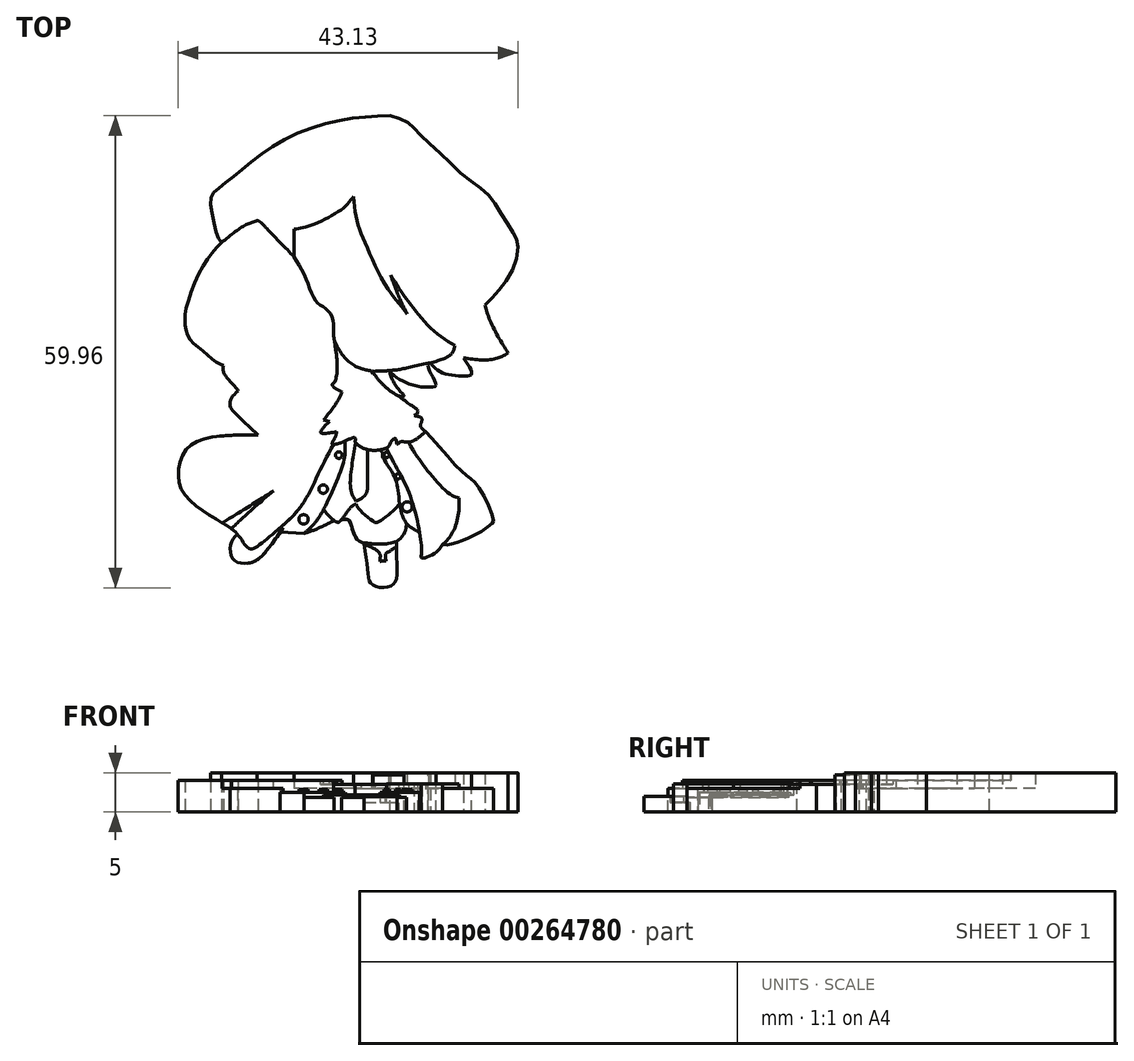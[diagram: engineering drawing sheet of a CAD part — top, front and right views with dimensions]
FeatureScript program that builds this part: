
annotation { "Feature Type Name" : "Feature", "Feature Type Description" : "" }
export const myFeature = defineFeature(function(context is Context, id is Id, definition is map)
    precondition{}
    {
        {
            var Q0;
            Q0=qCreatedBy(makeId("Top.planeOp"),FACE);
            var sketch = newSketch(context, id + "F0", { "sketchPlane" : qUnion([Q0])});
            skFitSpline(sketch, "E0", {"points": [v(4.64, 28.75) * mm, v(-1.15, 28.28) * mm, v(-8.48, 25.89) * mm, v(-13.76, 22.25) * mm, v(-16.76, 19.8) * mm, v(-18, 18.6) * mm, v(-18, 16.71) * mm, v(-17.3, 13.62) * mm, v(-16.76, 12.62) * mm], "startDerivative": vector(-35.2, -1.01) * mm, "endDerivative": vector(8.06, -11.5) * mm});
            skFitSpline(sketch, "E1", {"points": [v(4.64, 28.75) * mm, v(6.83, 27.93) * mm, v(8.08, 26.74) * mm, v(10.87, 24.14) * mm, v(14.46, 20.8) * mm, v(17.05, 18.8) * mm, v(18.75, 16.36) * mm, v(20.34, 13.82) * mm, v(20.87, 12.62) * mm, v(20.4, 9.58) * mm, v(18.5, 6.6) * mm, v(16.7, 4.7) * mm], "startDerivative": vector(29.85, -8.31) * mm, "endDerivative": vector(-20.54, -20.46) * mm});
            skFitSpline(sketch, "E2", {"points": [v(16.7, 4.7) * mm, v(17.2, 3.15) * mm, v(18.33, 0.8) * mm, v(19.68, -1.42) * mm], "startDerivative": vector(1.46, -5.18) * mm, "endDerivative": vector(3.8, -6.03) * mm});
            skFitSpline(sketch, "E3", {"points": [v(19.68, -1.42) * mm, v(17.58, -2.22) * mm, v(13.97, -2) * mm], "startDerivative": vector(-4.38, -2.29) * mm, "endDerivative": vector(-6.92, 0.99) * mm});
            skFitSpline(sketch, "E4", {"points": [v(13.97, -2) * mm, v(15.02, -4.06) * mm, v(13.97, -4.31) * mm, v(11.2, -3.85) * mm, v(9.78, -2.63) * mm], "startDerivative": vector(6.52, -9.38) * mm, "endDerivative": vector(-4.86, 5.7) * mm});
            skFitSpline(sketch, "E5", {"points": [v(9.78, -2.63) * mm, v(9.78, -3.85) * mm, v(10.47, -5.36) * mm, v(10.17, -5.69) * mm, v(7.8, -5.51) * mm, v(5.88, -4.69) * mm, v(4.64, -3.85) * mm], "startDerivative": vector(-1.49, -7.5) * mm, "endDerivative": vector(-7.08, 5.05) * mm});
            skFitSpline(sketch, "E6", {"points": [v(4.64, -3.85) * mm, v(5.08, -5.01) * mm, v(6, -6.31) * mm, v(6.46, -6.83) * mm, v(6.03, -6.9) * mm, v(5.2, -6.56) * mm, v(3.76, -5.41) * mm, v(2.5, -3.85) * mm], "startDerivative": vector(1.06, -6.43) * mm, "endDerivative": vector(-5.82, 7.97) * mm});
            skFitSpline(sketch, "E7", {"points": [v(0, 18.5) * mm, v(-1.53, 16.84) * mm, v(-5.52, 14.8) * mm, v(-7.53, 14.34) * mm], "startDerivative": vector(-4, -5.51) * mm, "endDerivative": vector(-6.25, -0.93) * mm});
            skFitSpline(sketch, "E8", {"points": [v(-7.53, 14.34) * mm, v(-7.53, 12.2) * mm, v(-7.53, 10.78) * mm], "startDerivative": vector(0, -4.1) * mm, "endDerivative": vector(0, -2.99) * mm});
            skFitSpline(sketch, "E9", {"points": [v(0, 18.5) * mm, v(0.48, 15.42) * mm, v(1.45, 12.73) * mm, v(3.73, 7.84) * mm, v(6.85, 3.57) * mm], "startDerivative": vector(1.71, -14.72) * mm, "endDerivative": vector(11.53, -14.1) * mm});
            skFitSpline(sketch, "E10", {"points": [v(6.85, 3.57) * mm, v(5.88, 5.54) * mm, v(4.73, 8.54) * mm], "startDerivative": vector(-2.16, 4.1) * mm, "endDerivative": vector(-2.07, 5.78) * mm});
            skFitSpline(sketch, "E11", {"points": [v(4.73, 8.54) * mm, v(6.2, 6.2) * mm, v(7.9, 3.96) * mm, v(10.12, 1.5) * mm, v(12.69, -0.3) * mm, v(14.43, -1.02) * mm], "startDerivative": vector(7.16, -11.83) * mm, "endDerivative": vector(10.1, -3.6) * mm});
            skFitSpline(sketch, "E12", {"points": [v(14.43, -1.02) * mm, v(13.9, 1.72) * mm, v(13.69, 3.12) * mm], "startDerivative": vector(-1, 5.08) * mm, "endDerivative": vector(-0.47, 3.08) * mm});
            skFitSpline(sketch, "E13", {"points": [v(13.83, 2.2) * mm, v(14.8, 1.45) * mm, v(16.53, 0.57) * mm], "startDerivative": vector(2, -1.71) * mm, "endDerivative": vector(3.34, -1.54) * mm});
            skFitSpline(sketch, "E14", {"points": [v(12.9, -0.4) * mm, v(12.41, -1.55) * mm, v(9.78, -2.63) * mm, v(5.88, -3.5) * mm, v(4.5, -3.63) * mm], "startDerivative": vector(-1.37, -6.6) * mm, "endDerivative": vector(-6.04, -0.38) * mm});
            skFitSpline(sketch, "E15", {"points": [v(4.64, -3.85) * mm, v(4.5, -3.63) * mm], "startDerivative": vector(-0.14, 0.22) * mm, "endDerivative": vector(-0.14, 0.22) * mm});
            skFitSpline(sketch, "E16", {"points": [v(4.5, -3.63) * mm, v(2.81, -3.7) * mm, v(2.45, -3.7) * mm], "startDerivative": vector(-2.92, -0.14) * mm, "endDerivative": vector(-0.94, 0.02) * mm});
            skFitSpline(sketch, "E17", {"points": [v(2.5, -3.85) * mm, v(2.45, -3.7) * mm], "startDerivative": vector(-0.04, 0.14) * mm, "endDerivative": vector(-0.04, 0.14) * mm});
            skFitSpline(sketch, "E18", {"points": [v(2.45, -3.7) * mm, v(1, -3.37) * mm, v(-0.99, -2.1) * mm, v(-2.34, 0) * mm, v(-2.42, 0.26) * mm, v(-2.5, 0.86) * mm], "startDerivative": vector(-6.7, 1.33) * mm, "endDerivative": vector(-0.3, 5.17) * mm});
            skFitSpline(sketch, "E19", {"points": [v(-2.5, 0.86) * mm, v(-2.5, 1.74) * mm, v(-2.76, 3.31) * mm, v(-3.77, 4.43) * mm, v(-4.85, 5.32) * mm, v(-6, 8) * mm, v(-7.53, 10.78) * mm, v(-9.09, 12.43) * mm, v(-10.9, 14.33) * mm, v(-11.48, 14.95) * mm, v(-12.22, 15.42) * mm], "startDerivative": vector(0.15, 11.14) * mm, "endDerivative": vector(-6.01, -4.13) * mm});
            skFitSpline(sketch, "E20", {"points": [v(-12.22, 15.42) * mm, v(-13.92, 14.74) * mm, v(-16.76, 12.62) * mm], "startDerivative": vector(-3.9, -1.2) * mm, "endDerivative": vector(-5.1, -4.23) * mm});
            skFitSpline(sketch, "E21", {"points": [v(-16.76, 12.62) * mm, v(-19.1, 9.65) * mm, v(-21.19, 4.46) * mm, v(-21.36, 2.17) * mm, v(-20.87, 0.51) * mm, v(-19.28, -0.97) * mm, v(-17.48, -2.47) * mm, v(-16.51, -2.98) * mm], "startDerivative": vector(-13.81, -14.7) * mm, "endDerivative": vector(9.8, -4.22) * mm});
            skFitSpline(sketch, "E22", {"points": [v(-16.51, -2.98) * mm, v(-16.51, -3.71) * mm, v(-15.97, -4.63) * mm, v(-14.72, -6.03) * mm, v(-14.3, -6.84) * mm, v(-14.16, -7.62) * mm], "startDerivative": vector(-0.5, -4.39) * mm, "endDerivative": vector(0.62, -4.57) * mm});
            skFitSpline(sketch, "E23", {"points": [v(-14.62, -6.18) * mm, v(-15.58, -7.28) * mm, v(-15.62, -8.19) * mm, v(-15.2, -8.81) * mm, v(-14.09, -9.93) * mm, v(-12.13, -11.8) * mm], "startDerivative": vector(-5.87, -5.15) * mm, "endDerivative": vector(7.41, -7.05) * mm});
            skFitSpline(sketch, "E24", {"points": [v(-12.13, -11.8) * mm, v(-14.56, -11.8) * mm, v(-18.73, -12.25) * mm, v(-21.2, -13.6) * mm, v(-22.17, -16.09) * mm, v(-21.84, -18.7) * mm, v(-19.67, -21.03) * mm, v(-16.76, -22.9) * mm, v(-14.56, -24.6) * mm, v(-13.17, -26.29) * mm, v(-11.3, -25.24) * mm, v(-6.96, -21.25) * mm, v(-4.17, -16.16) * mm, v(-1.46, -10.56) * mm, v(-0.58, -6.65) * mm], "startDerivative": vector(-37.16, 0.62) * mm, "endDerivative": vector(7.21, 49.15) * mm});
            skFitSpline(sketch, "E25", {"points": [v(-0.58, -6.65) * mm, v(-2.34, 0) * mm], "startDerivative": vector(-1.76, 6.65) * mm, "endDerivative": vector(-1.76, 6.65) * mm});
            skFitSpline(sketch, "E26", {"points": [v(5.2, -6.56) * mm, v(7.5, -9.23) * mm, v(8.63, -9.61) * mm, v(8.63, -10.23) * mm, v(8.5, -10.63) * mm, v(9.43, -11.65) * mm, v(13.44, -16.1) * mm, v(14.88, -17.31) * mm, v(16.24, -18.94) * mm, v(17.82, -22.63) * mm, v(17.58, -23.1) * mm, v(15.58, -24.42) * mm, v(13.75, -25.24) * mm, v(12.28, -25.72) * mm, v(11.34, -25.72) * mm], "startDerivative": vector(22.11, -34.49) * mm, "endDerivative": vector(-17.24, 1.6) * mm});
            skFitSpline(sketch, "E27", {"points": [v(11.34, -25.72) * mm, v(10.38, -26.8) * mm, v(8.7, -27.42) * mm, v(8.65, -26.96) * mm, v(8.4, -24.04) * mm, v(6.68, -18.2) * mm, v(4.23, -13.53) * mm, v(1, -3.37) * mm], "startDerivative": vector(-7.19, -11.67) * mm, "endDerivative": vector(-12.38, 45.63) * mm});
            skFitSpline(sketch, "E28", {"points": [v(11.34, -25.72) * mm, v(12.16, -24.9) * mm, v(13.2, -22.66) * mm, v(13.45, -19.83) * mm], "startDerivative": vector(3.27, 2.7) * mm, "endDerivative": vector(0.06, 7.34) * mm});
            skFitSpline(sketch, "E29", {"points": [v(13.45, -19.83) * mm, v(12.34, -19.36) * mm, v(9.74, -16.71) * mm, v(7.36, -13.34) * mm, v(2.33, -3.68) * mm], "startDerivative": vector(-7.77, 2.03) * mm, "endDerivative": vector(-13.93, 27.93) * mm});
            skFitSpline(sketch, "E30", {"points": [v(-2.45, 0.44) * mm, v(-2.05, -3.03) * mm, v(-2.31, -4.91) * mm, v(-2.72, -5.42) * mm], "startDerivative": vector(1.24, -7.85) * mm, "endDerivative": vector(-2.26, -2.02) * mm});
            skFitSpline(sketch, "E31", {"points": [v(-2.72, -5.42) * mm, v(-2.34, -5.85) * mm, v(-1.44, -6.32) * mm], "startDerivative": vector(0.75, -1.04) * mm, "endDerivative": vector(1.78, -0.78) * mm});
            skFitSpline(sketch, "E32", {"points": [v(-1.44, -6.32) * mm, v(-2, -7.48) * mm, v(-3.76, -9.9) * mm], "startDerivative": vector(-1.13, -2.7) * mm, "endDerivative": vector(-3.36, -4.35) * mm});
            skFitSpline(sketch, "E33", {"points": [v(-3.76, -9.9) * mm, v(-3, -10.06) * mm], "startDerivative": vector(0.75, -0.16) * mm, "endDerivative": vector(0.75, -0.16) * mm});
            skFitSpline(sketch, "E34", {"points": [v(-3, -10.06) * mm, v(-3.93, -11.03) * mm, v(-4.14, -11.5) * mm, v(-3.76, -11.6) * mm, v(-2.1, -11.38) * mm], "startDerivative": vector(-3.38, -3.26) * mm, "endDerivative": vector(5.48, 1) * mm});
            skFitSpline(sketch, "E35", {"points": [v(-2.1, -11.38) * mm, v(-2.44, -12.36) * mm, v(-2.7, -12.92) * mm, v(-1.52, -12.77) * mm, v(0.19, -12.16) * mm, v(0.27, -12.46) * mm, v(0.22, -12.62) * mm, v(1.68, -13.63) * mm, v(4.4, -13.34) * mm, v(4.69, -12.84) * mm, v(5.32, -12.23) * mm, v(5.47, -12.67) * mm, v(5.61, -12.97) * mm, v(5.96, -12.7) * mm, v(7, -12.7) * mm, v(8.57, -11.9) * mm, v(9.82, -10.47) * mm, v(9.68, -10.31) * mm], "startDerivative": vector(-3.85, -15.8) * mm, "endDerivative": vector(-7.4, 3.88) * mm});
            skFitSpline(sketch, "E36", {"points": [v(9.68, -10.31) * mm, v(8.98, -10.31) * mm, v(7.23, -10) * mm, v(6.43, -9.7) * mm], "startDerivative": vector(-2.2, -0.14) * mm, "endDerivative": vector(-2.27, 0.96) * mm});
            skFitSpline(sketch, "E37", {"points": [v(6.4, -9.7) * mm, v(7.06, -9.46) * mm, v(8.04, -9.14) * mm, v(8.15, -8.64) * mm, v(7.57, -8.17) * mm, v(5.73, -6.83) * mm], "startDerivative": vector(3.4, 1.59) * mm, "endDerivative": vector(-6.64, 5.1) * mm});
            skFitSpline(sketch, "E38", {"points": [v(-1.44, -6.32) * mm, v(-0.6, -4.07) * mm, v(-0.42, -3.64) * mm, v(2.26, -3.9) * mm, v(2.8, -4.27) * mm], "startDerivative": vector(3.4, 7.98) * mm, "endDerivative": vector(1.85, -2.14) * mm});
            skFitSpline(sketch, "E39", {"points": [v(-9.93, -24.12) * mm, v(-6.25, -24.29) * mm], "startDerivative": vector(3.69, -0.17) * mm, "endDerivative": vector(3.69, -0.17) * mm});
            skFitSpline(sketch, "E40", {"points": [v(-6.25, -24.29) * mm, v(-4.6, -22.6) * mm, v(-2.34, -18.2) * mm, v(-1.08, -14.43) * mm, v(-1.08, -12.58) * mm], "startDerivative": vector(7.6, 6.43) * mm, "endDerivative": vector(-0.8, 8.96) * mm});
            skFitSpline(sketch, "E41", {"points": [v(3.37, -13.69) * mm, v(3.72, -14.15) * mm, v(3.7, -14.48) * mm, v(5.04, -16.72) * mm, v(5.73, -19.28) * mm, v(6.56, -22.74) * mm, v(8.43, -24.17) * mm], "startDerivative": vector(5.17, -5.25) * mm, "endDerivative": vector(11.12, -5.53) * mm});
            skFitSpline(sketch, "E42", {"points": [v(-3.76, -21.23) * mm, v(-3.15, -22.03) * mm, v(-2.05, -22.88) * mm, v(-1.52, -22.58) * mm, v(-0.22, -20.9) * mm, v(0.32, -20.56) * mm], "startDerivative": vector(2.47, -3.74) * mm, "endDerivative": vector(2.9, 1.37) * mm});
            skFitSpline(sketch, "E43", {"points": [v(0.32, -20.56) * mm, v(0.86, -21.38) * mm, v(2.7, -22.88) * mm, v(3.12, -22.88) * mm, v(4.77, -21.7) * mm, v(5.9, -20.56) * mm], "startDerivative": vector(2.06, -4.3) * mm, "endDerivative": vector(4.48, 5.02) * mm});
            skFitSpline(sketch, "E44", {"points": [v(0.32, -20.56) * mm, v(-0.2, -19.43) * mm, v(-0.22, -17.63) * mm, v(0, -14.09) * mm, v(0.22, -12.62) * mm], "startDerivative": vector(-3.18, 5.39) * mm, "endDerivative": vector(1.1, 5.7) * mm});
            skFitSpline(sketch, "E45", {"points": [v(1.84, -13.67) * mm, v(1.68, -19.06) * mm, v(1.23, -19.88) * mm, v(0.32, -20.56) * mm], "startDerivative": vector(0.2, -12.39) * mm, "endDerivative": vector(-4.1, -2.8) * mm});
            skFitSpline(sketch, "E46", {"points": [v(-6.25, -24.29) * mm, v(-4.72, -23.77) * mm, v(-2.46, -22.66) * mm], "startDerivative": vector(3.28, 1) * mm, "endDerivative": vector(4.25, 2.21) * mm});
            skFitSpline(sketch, "E47", {"points": [v(-1.52, -22.58) * mm, v(-0.63, -22.58) * mm, v(-0.2, -23.51) * mm, v(0.44, -25.02) * mm, v(1.44, -25.5) * mm, v(5.66, -25.22) * mm, v(6.72, -23.47) * mm, v(6.77, -23.02) * mm], "startDerivative": vector(10.67, 1.95) * mm, "endDerivative": vector(0.05, 4.54) * mm});
            skSolve(sketch);
        }
        {
            var Q0;
            Q0=makeQuery(id+"F0.imprint","IMPRINT",FACE,{"disambiguationData":[TD([[makeQuery(id+"F0.imprint","IMPRINT",EDGE,{"derivedFrom":sQuery(id+"F0.wireOp",EDGE,"E7")}),1.0]])]});
            extrude(context, id + "F1", {"entities" : qUnion([Q0]), "depth" : 3 * mm, "offsetDistance" : 25 * mm});
        }
        {
            var Q0;
            Q0=makeQuery(id+"F0.imprint","IMPRINT",FACE,{"disambiguationData":[TD([[makeQuery(id+"F0.imprint","IMPRINT",EDGE,{"derivedFrom":sQuery(id+"F0.wireOp",EDGE,"E0")}),1.0]])]});
            extrude(context, id + "F2", {"entities" : qUnion([Q0]), "operationType" : NewBodyOperationType.ADD, "depth" : 5 * mm, "offsetDistance" : 25 * mm});
        }
        {
            var Q0;
            {var subQ0=sQuery(id+"F0.wireOp",EDGE,"E20");Q0=makeQuery(id+"F0.imprint","IMPRINT",FACE,{"disambiguationData":[TD([[makeQuery(id+"F0.imprint","IMPRINT",EDGE,{"derivedFrom":subQ0}),1.0]])]});}
            var Q1;
            {var subQ0=sQuery(id+"F0.wireOp",EDGE,"E27");Q1=makeQuery(id+"F0.imprint","IMPRINT",FACE,{"disambiguationData":[TD([[makeQuery(id+"F0.imprint","IMPRINT",EDGE,{"derivedFrom":subQ0}),-1.0]])]});}
            extrude(context, id + "F3", {"entities" : qUnion([Q0, Q1]), "operationType" : NewBodyOperationType.ADD, "depth" : 4 * mm, "offsetDistance" : 25 * mm});
        }
        {
            var Q0;
            {var subQ0=sQuery(id+"F0.wireOp",EDGE,"E28");Q0=makeQuery(id+"F0.imprint","IMPRINT",FACE,{"disambiguationData":[TD([[makeQuery(id+"F0.imprint","IMPRINT",EDGE,{"derivedFrom":subQ0}),-1.0]])]});}
            var Q1;
            {var subQ1=sQuery(id+"F0.wireOp",EDGE,"E17");Q1=makeQuery(id+"F0.imprint","IMPRINT",FACE,{"disambiguationData":[TD([[makeQuery(id+"F0.imprint","IMPRINT",EDGE,{"derivedFrom":subQ1}),1.0]])]});}
            extrude(context, id + "F4", {"entities" : qUnion([Q0, Q1]), "operationType" : NewBodyOperationType.ADD, "depth" : 3 * mm, "offsetDistance" : 25 * mm});
        }
        {
            var Q0;
            {var subQ5=sQuery(id+"F0.wireOp",EDGE,"E25");var subQ6=sQuery(id+"F0.wireOp",EDGE,"E24");var subQ7=makeQuery(id+"F0.imprint","INTERSECT",VERTEX,{"derivedFrom":[subQ6,subQ5]});Q0=makeQuery(id+"F0.imprint","IMPRINT",FACE,{"disambiguationData":[TD([[makeQuery(id+"F0.imprint","IMPRINT",EDGE,{"disambiguationData":[TD([[subQ7,1.0]])],"derivedFrom":subQ6}),-1.0]])]});}
            var Q1;
            {var subQ0=sQuery(id+"F0.wireOp",EDGE,"E32");Q1=makeQuery(id+"F0.imprint","IMPRINT",FACE,{"disambiguationData":[TD([[makeQuery(id+"F0.imprint","IMPRINT",EDGE,{"derivedFrom":subQ0}),1.0]])]});}
            var Q2;
            Q2=makeQuery(id+"F3.opExtrude","CAP_FACE",FACE,{"disambiguationData":[OSD([sQuery(id+"F0.wireOp",EDGE,"E18"),sQuery(id+"F0.wireOp",EDGE,"E27"),sQuery(id+"F0.wireOp",EDGE,"E28"),sQuery(id+"F0.wireOp",EDGE,"E29")])],"isStart":false});
            var Q3;
            {var subQ0=sQuery(id+"F0.wireOp",EDGE,"E26");var subQ5=sQuery(id+"F0.wireOp",EDGE,"E6");var subQ6=makeQuery(id+"F0.imprint","INTERSECT",VERTEX,{"derivedFrom":[subQ5,subQ0]});Q3=makeQuery(id+"F0.imprint","IMPRINT",FACE,{"disambiguationData":[TD([[makeQuery(id+"F0.imprint","IMPRINT",EDGE,{"disambiguationData":[TD([[subQ6,-1.0]])],"derivedFrom":subQ5}),1.0]])]});}
            var Q4;
            {var subQ0=sQuery(id+"F0.wireOp",EDGE,"E26");var subQ1=sQuery(id+"F0.wireOp",EDGE,"E6");var subQ2=makeQuery(id+"F0.imprint","INTERSECT",VERTEX,{"derivedFrom":[subQ1,subQ0]});Q4=makeQuery(id+"F0.imprint","IMPRINT",FACE,{"disambiguationData":[TD([[makeQuery(id+"F0.imprint","IMPRINT",EDGE,{"disambiguationData":[TD([[subQ2,1.0]])],"derivedFrom":subQ1}),1.0]])]});}
            var Q5;
            {var subQ4=sQuery(id+"F0.wireOp",EDGE,"E30");Q5=makeQuery(id+"F0.imprint","IMPRINT",FACE,{"disambiguationData":[TD([[makeQuery(id+"F0.imprint","IMPRINT",EDGE,{"derivedFrom":subQ4}),1.0]])]});}
            var Q6;
            {var subQ0=sQuery(id+"F0.wireOp",EDGE,"E25");var subQ1=sQuery(id+"F0.wireOp",EDGE,"E18");var subQ2=makeQuery(id+"F0.imprint","INTERSECT",VERTEX,{"derivedFrom":[subQ1,subQ0]});Q6=makeQuery(id+"F0.imprint","IMPRINT",FACE,{"disambiguationData":[TD([[makeQuery(id+"F0.imprint","IMPRINT",EDGE,{"disambiguationData":[TD([[subQ2,1.0]])],"derivedFrom":subQ1}),1.0]])]});}
            extrude(context, id + "F5", {"entities" : qUnion([Q0, Q1, Q2, Q3, Q4, Q5, Q6]), "operationType" : NewBodyOperationType.ADD, "depth" : 5 * mm, "offsetDistance" : 25 * mm});
        }
        {
            var Q0;
            Q0=makeQuery(id+"F5.opExtrude","CAP_FACE",FACE,{"disambiguationData":[OSD([sQuery(id+"F0.wireOp",EDGE,"E18"),sQuery(id+"F0.wireOp",EDGE,"E27"),sQuery(id+"F0.wireOp",EDGE,"E28"),sQuery(id+"F0.wireOp",EDGE,"E29")])],"isStart":false});
            extrude(context, id + "F6", {"entities" : qUnion([Q0]), "operationType" : NewBodyOperationType.REMOVE, "oppositeDirection" : true, "depth" : 5.4 * mm, "offsetDistance" : 25 * mm});
        }
        {
            var Q0;
            {var subQ0=sQuery(id+"F0.wireOp",EDGE,"E35");var subQ1=sQuery(id+"F0.wireOp",EDGE,"E27");var subQ2=makeQuery(id+"F0.imprint","INTERSECT",VERTEX,{"derivedFrom":[subQ1,subQ0]});Q0=makeQuery(id+"F0.imprint","IMPRINT",FACE,{"disambiguationData":[TD([[makeQuery(id+"F0.imprint","IMPRINT",EDGE,{"disambiguationData":[TD([[subQ2,-1.0]])],"derivedFrom":subQ1}),-1.0]])]});}
            extrude(context, id + "F7", {"entities" : qUnion([Q0]), "operationType" : NewBodyOperationType.ADD, "depth" : 5 * mm, "offsetDistance" : 25 * mm});
        }
        {
            var Q0;
            {var subQ0=sQuery(id+"F0.wireOp",EDGE,"E39");Q0=makeQuery(id+"F0.imprint","IMPRINT",FACE,{"disambiguationData":[TD([[makeQuery(id+"F0.imprint","IMPRINT",EDGE,{"derivedFrom":subQ0}),1.0]])]});}
            var Q1;
            {var subQ0=sQuery(id+"F0.wireOp",EDGE,"E41");var subQ5=sQuery(id+"F0.wireOp",EDGE,"E27");var subQ7=makeQuery(id+"F0.imprint","INTERSECT",VERTEX,{"derivedFrom":[subQ5,subQ0]});Q1=makeQuery(id+"F0.imprint","IMPRINT",FACE,{"disambiguationData":[TD([[makeQuery(id+"F0.imprint","IMPRINT",EDGE,{"disambiguationData":[TD([[subQ7,-1.0]])],"derivedFrom":subQ5}),1.0]])]});}
            extrude(context, id + "F8", {"entities" : qUnion([Q0, Q1]), "operationType" : NewBodyOperationType.ADD, "depth" : 2.5 * mm, "offsetDistance" : 25 * mm});
        }
        {
            var Q0;
            {var subQ0=sQuery(id+"F0.wireOp",EDGE,"E46");Q0=makeQuery(id+"F0.imprint","IMPRINT",FACE,{"disambiguationData":[TD([[makeQuery(id+"F0.imprint","IMPRINT",EDGE,{"derivedFrom":subQ0}),1.0]])]});}
            var Q1;
            {var subQ0=sQuery(id+"F0.wireOp",EDGE,"E43");Q1=makeQuery(id+"F0.imprint","IMPRINT",FACE,{"disambiguationData":[TD([[makeQuery(id+"F0.imprint","IMPRINT",EDGE,{"derivedFrom":subQ0}),-1.0]])]});}
            extrude(context, id + "F9", {"entities" : qUnion([Q0, Q1]), "operationType" : NewBodyOperationType.ADD, "depth" : 1.9 * mm, "offsetDistance" : 25 * mm});
        }
        {
            var Q0;
            {var subQ7=sQuery(id+"F0.wireOp",EDGE,"E44");Q0=makeQuery(id+"F0.imprint","IMPRINT",FACE,{"disambiguationData":[TD([[makeQuery(id+"F0.imprint","IMPRINT",EDGE,{"derivedFrom":subQ7}),1.0]])]});}
            var Q1;
            {var subQ0=sQuery(id+"F0.wireOp",EDGE,"E44");Q1=makeQuery(id+"F0.imprint","IMPRINT",FACE,{"disambiguationData":[TD([[makeQuery(id+"F0.imprint","IMPRINT",EDGE,{"derivedFrom":subQ0}),-1.0]])]});}
            var Q2;
            {var subQ4=sQuery(id+"F0.wireOp",EDGE,"E43");Q2=makeQuery(id+"F0.imprint","IMPRINT",FACE,{"disambiguationData":[TD([[makeQuery(id+"F0.imprint","IMPRINT",EDGE,{"derivedFrom":subQ4}),1.0]])]});}
            extrude(context, id + "F10", {"entities" : qUnion([Q0, Q1, Q2]), "operationType" : NewBodyOperationType.ADD, "depth" : 2.2 * mm, "offsetDistance" : 25 * mm});
        }
        {
            var Q0;
            Q0=makeQuery(id+"F10.opExtrude","CAP_FACE",FACE,{"disambiguationData":[OSD([sQuery(id+"F0.wireOp",EDGE,"E35"),sQuery(id+"F0.wireOp",EDGE,"E40"),sQuery(id+"F0.wireOp",EDGE,"E41"),sQuery(id+"F0.wireOp",EDGE,"E42"),sQuery(id+"F0.wireOp",EDGE,"E43")])],"isStart":false});
            var sketch = newSketch(context, id + "F11", { "sketchPlane" : qUnion([Q0])});
            skFitSpline(sketch, "E48", {"points": [v(0.31, -12.79) * mm, v(0, -14.3) * mm, v(-0.3, -18.86) * mm, v(0.32, -20.56) * mm], "startDerivative": vector(-1.12, -4.6) * mm, "endDerivative": vector(2.78, -4.78) * mm, "construction": true});
            skFitSpline(sketch, "E49", {"points": [v(0.32, -20.56) * mm, v(1.37, -19.7) * mm, v(1.74, -18.65) * mm, v(1.78, -13.66) * mm], "startDerivative": vector(4.62, 3.23) * mm, "endDerivative": vector(-0.2, 11.8) * mm, "construction": true});
            skFitSpline(sketch, "E50", {"points": [v(1.78, -13.66) * mm, v(1.32, -13.5) * mm, v(0.7, -13.15) * mm, v(0.31, -12.79) * mm], "startDerivative": vector(-1.43, 0.4) * mm, "endDerivative": vector(-1.08, 1.14) * mm});
            skFitSpline(sketch, "E51", {"points": [v(0.31, -12.79) * mm, v(-0.24, -16.09) * mm, v(-0.3, -18.86) * mm, v(0.31, -20.22) * mm], "startDerivative": vector(-1.58, -8.5) * mm, "endDerivative": vector(2.92, -4.7) * mm});
            skFitSpline(sketch, "E52", {"points": [v(0.31, -20.22) * mm, v(1.6, -19.29) * mm, v(1.8, -17.41) * mm, v(1.78, -13.66) * mm], "startDerivative": vector(5.65, 2.8) * mm, "endDerivative": vector(0.11, 9.44) * mm});
            skSolve(sketch);
        }
        {
            var Q0;
            {var subQ0=sQuery(id+"F11.wireOp",EDGE,"E51");Q0=makeQuery(id+"F11.imprint","IMPRINT",FACE,{"disambiguationData":[TD([[makeQuery(id+"F11.imprint","IMPRINT",EDGE,{"derivedFrom":subQ0}),1.0]])]});}
            extrude(context, id + "F12", {"entities" : qUnion([Q0]), "operationType" : NewBodyOperationType.REMOVE, "oppositeDirection" : true, "depth" : .3 * mm, "offsetDistance" : 25 * mm});
        }
        {
            var Q0;
            Q0=qCreatedBy(makeId("Top.planeOp"),FACE);
            var sketch = newSketch(context, id + "F13", { "sketchPlane" : qUnion([Q0])});
            skFitSpline(sketch, "E53", {"points": [v(9.52, -2.65) * mm, v(9.76, -3.8) * mm, v(10.5, -5.37) * mm, v(10.18, -5.68) * mm, v(7.75, -5.53) * mm, v(5.85, -4.72) * mm, v(4.63, -3.84) * mm, v(4.5, -3.63) * mm], "startDerivative": vector(-1.3, -7.93) * mm, "endDerivative": vector(-1.34, 2.86) * mm});
            skFitSpline(sketch, "E54", {"points": [v(4.5, -3.63) * mm, v(5.85, -3.47) * mm, v(9.52, -2.65) * mm], "startDerivative": vector(3.2, 0.24) * mm, "endDerivative": vector(6.92, 1.68) * mm});
            skFitSpline(sketch, "E55", {"points": [v(4.63, -3.84) * mm, v(5.06, -4.99) * mm, v(6.05, -6.32) * mm, v(6.48, -6.85) * mm, v(6.01, -6.9) * mm, v(4.39, -5.92) * mm, v(2.46, -3.69) * mm], "startDerivative": vector(2.06, -7.14) * mm, "endDerivative": vector(-7.59, 9.82) * mm});
            skFitSpline(sketch, "E56", {"points": [v(2.46, -3.69) * mm, v(4.5, -3.63) * mm], "startDerivative": vector(2.03, 0.06) * mm, "endDerivative": vector(2.03, 0.06) * mm});
            skSolve(sketch);
        }
        {
            var Q0;
            {var subQ5=sQuery(id+"F0.wireOp",EDGE,"E15");Q0=makeQuery(id+"F0.imprint","IMPRINT",FACE,{"disambiguationData":[TD([[makeQuery(id+"F0.imprint","IMPRINT",EDGE,{"derivedFrom":subQ5}),1.0]])]});}
            extrude(context, id + "F14", {"entities" : qUnion([Q0]), "operationType" : NewBodyOperationType.ADD, "depth" : 4.7 * mm, "offsetDistance" : 25 * mm});
        }
        {
            var Q0;
            Q0=qCreatedBy(makeId("Top.planeOp"),FACE);
            var sketch = newSketch(context, id + "F15", { "sketchPlane" : qUnion([Q0])});
            skFitSpline(sketch, "E57", {"points": [v(1, -3.37) * mm, v(1.66, -3.54) * mm, v(2.34, -3.67) * mm], "startDerivative": vector(1.3, -0.37) * mm, "endDerivative": vector(1.36, -0.24) * mm});
            skFitSpline(sketch, "E58", {"points": [v(2.34, -3.67) * mm, v(2.53, -4.06) * mm], "startDerivative": vector(0.2, -0.39) * mm, "endDerivative": vector(0.2, -0.39) * mm});
            skFitSpline(sketch, "E59", {"points": [v(1, -3.37) * mm, v(1.05, -3.74) * mm], "startDerivative": vector(0.05, -0.38) * mm, "endDerivative": vector(0.05, -0.38) * mm});
            skFitSpline(sketch, "E60", {"points": [v(1.05, -3.74) * mm, v(2.53, -4.06) * mm], "startDerivative": vector(1.48, -0.31) * mm, "endDerivative": vector(1.48, -0.31) * mm});
            skSolve(sketch);
        }
        {
            var Q0;
            Q0=makeQuery(id+"F15.imprint","IMPRINT",FACE,{"disambiguationData":[TD([[makeQuery(id+"F15.imprint","IMPRINT",EDGE,{"derivedFrom":sQuery(id+"F15.wireOp",EDGE,"E57")}),-1.0]])]});
            extrude(context, id + "F16", {"entities" : qUnion([Q0]), "operationType" : NewBodyOperationType.ADD, "depth" : 5 * mm, "offsetDistance" : 25 * mm});
        }
        {
            var Q0;
            {var subQ0=sQuery(id+"F13.wireOp",EDGE,"E54");Q0=makeQuery(id+"F13.imprint","IMPRINT",FACE,{"disambiguationData":[TD([[makeQuery(id+"F13.imprint","IMPRINT",EDGE,{"derivedFrom":subQ0}),-1.0]])]});}
            extrude(context, id + "F17", {"entities" : qUnion([Q0]), "operationType" : NewBodyOperationType.ADD, "depth" : 5 * mm, "offsetDistance" : 25 * mm});
        }
        {
            var Q0;
            {var subQ0=sQuery(id+"F0.wireOp",EDGE,"E38");var subQ1=sQuery(id+"F0.wireOp",EDGE,"E35");var subQ2=sQuery(id+"F0.wireOp",EDGE,"E29");var subQ3=sQuery(id+"F0.wireOp",EDGE,"E27");Q0=makeQuery(id+"F16.boolean.opBoolean","MERGE",FACE,{"derivedFrom":[makeQuery(id+"F7.boolean.opBoolean","MERGE",FACE,{"derivedFrom":[makeQuery(id+"F5.opExtrude","CAP_FACE",FACE,{"disambiguationData":[OSD([sQuery(id+"F0.wireOp",EDGE,"E6"),sQuery(id+"F0.wireOp",EDGE,"E26"),subQ2,subQ1,sQuery(id+"F0.wireOp",EDGE,"E37"),subQ0])],"isStart":false}),makeQuery(id+"F5.opExtrude","CAP_FACE",FACE,{"disambiguationData":[OSD([sQuery(id+"F0.wireOp",EDGE,"E18"),subQ3,sQuery(id+"F0.wireOp",EDGE,"E30"),sQuery(id+"F0.wireOp",EDGE,"E31"),sQuery(id+"F0.wireOp",EDGE,"E32"),sQuery(id+"F0.wireOp",EDGE,"E33"),sQuery(id+"F0.wireOp",EDGE,"E34"),subQ1])],"isStart":false}),makeQuery(id+"F7.opExtrude","CAP_FACE",FACE,{"disambiguationData":[OSD([subQ3,subQ2,subQ1,subQ0])],"isStart":false})]}),makeQuery(id+"F16.opExtrude","CAP_FACE",FACE,{"disambiguationData":[OSD([sQuery(id+"F15.wireOp",EDGE,"E57"),sQuery(id+"F15.wireOp",EDGE,"E58"),sQuery(id+"F15.wireOp",EDGE,"E59"),sQuery(id+"F15.wireOp",EDGE,"E60")])],"isStart":false})]});}
            extrude(context, id + "F18", {"entities" : qUnion([Q0]), "operationType" : NewBodyOperationType.REMOVE, "oppositeDirection" : true, "depth" : 1.5 * mm, "offsetDistance" : 25 * mm});
        }
        {
            var Q0;
            Q0=qCreatedBy(makeId("Top.planeOp"),FACE);
            var sketch = newSketch(context, id + "F19", { "sketchPlane" : qUnion([Q0])});
            skCircle(sketch, "E61", {"center": v(-1.84, -14.36) * mm, "radius": 0.42 * mm});
            skCircle(sketch, "E62", {"center": v(-3.82, -18.68) * mm, "radius": 0.54 * mm});
            skCircle(sketch, "E63", {"center": v(-6.32, -22.52) * mm, "radius": 0.6 * mm});
            skCircle(sketch, "E64", {"center": v(4.22, -14.34) * mm, "radius": 0.35 * mm});
            skCircle(sketch, "E65", {"center": v(5.68, -17.06) * mm, "radius": 0.33 * mm});
            skCircle(sketch, "E66", {"center": v(6.83, -20.93) * mm, "radius": 0.64 * mm});
            skSolve(sketch);
        }
        {
            var Q0;
            Q0 = qSketchRegion(id + "F19", true);
            extrude(context, id + "F20", {"entities" : qUnion([Q0]), "operationType" : NewBodyOperationType.ADD, "depth" : 2.9 * mm, "offsetDistance" : 25 * mm});
        }
        {
            var Q0;
            Q0=qCreatedBy(makeId("Top.planeOp"),FACE);
            var sketch = newSketch(context, id + "F21", { "sketchPlane" : qUnion([Q0])});
            skFitSpline(sketch, "E67", {"points": [v(-14.54, -24.22) * mm, v(-15.42, -25.24) * mm, v(-15.61, -26.76) * mm, v(-14.92, -27.87) * mm, v(-13.25, -28.07) * mm, v(-11.73, -27.27) * mm, v(-8.9, -23.57) * mm], "startDerivative": vector(-7.27, -6.51) * mm, "endDerivative": vector(11.48, 16.89) * mm});
            skFitSpline(sketch, "E68", {"points": [v(-14.54, -24.22) * mm, v(-8.9, -23.57) * mm], "startDerivative": vector(5.63, 0.65) * mm, "endDerivative": vector(5.63, 0.65) * mm});
            skFitSpline(sketch, "E69", {"points": [v(1.38, -25.37) * mm, v(1.71, -28.05) * mm, v(2.07, -30.34) * mm, v(3.1, -31.05) * mm, v(4.32, -31.16) * mm, v(5.38, -30.38) * mm, v(5.4, -28.5) * mm, v(5.45, -25.53) * mm, v(5.3, -24.87) * mm], "startDerivative": vector(2.64, -16.73) * mm, "endDerivative": vector(-2.66, 6.46) * mm});
            skFitSpline(sketch, "E70", {"points": [v(1.38, -25.37) * mm, v(5.3, -24.87) * mm], "startDerivative": vector(3.91, 0.5) * mm, "endDerivative": vector(3.91, 0.5) * mm});
            skSolve(sketch);
        }
        {
            var Q0;
            Q0=makeQuery(id+"F21.imprint","IMPRINT",FACE,{"disambiguationData":[TD([[makeQuery(id+"F21.imprint","IMPRINT",EDGE,{"derivedFrom":sQuery(id+"F21.wireOp",EDGE,"E67")}),1.0]])]});
            extrude(context, id + "F22", {"entities" : qUnion([Q0]), "operationType" : NewBodyOperationType.ADD, "depth" : 3 * mm, "offsetDistance" : 25 * mm});
        }
        {
            var Q0;
            Q0=qCreatedBy(makeId("Top.planeOp"),FACE);
            var sketch = newSketch(context, id + "F23", { "sketchPlane" : qUnion([Q0])});
            skFitSpline(sketch, "E71", {"points": [v(1.3, -25.28) * mm, v(1.87, -29.43) * mm, v(2.17, -30.54) * mm, v(3.32, -31.2) * mm, v(4.92, -30.88) * mm, v(5.45, -30.08) * mm, v(5.49, -26.82) * mm, v(5.5, -25.07) * mm], "startDerivative": vector(3.21, -22.63) * mm, "endDerivative": vector(0.4, 10.97) * mm});
            skFitSpline(sketch, "E72", {"points": [v(1.3, -25.28) * mm, v(5.5, -25.07) * mm], "startDerivative": vector(4.2, 0.2) * mm, "endDerivative": vector(4.2, 0.2) * mm});
            skFitSpline(sketch, "E73", {"points": [v(1.36, -25.67) * mm, v(3.32, -26.8) * mm, v(3.39, -27.88) * mm], "startDerivative": vector(4.2, -1.71) * mm, "endDerivative": vector(-0.08, -3.4) * mm});
            skFitSpline(sketch, "E74", {"points": [v(3.39, -27.88) * mm, v(3.77, -27.8) * mm, v(4.18, -27.82) * mm], "startDerivative": vector(0.78, 0.22) * mm, "endDerivative": vector(0.82, -0.1) * mm});
            skFitSpline(sketch, "E75", {"points": [v(4.18, -27.82) * mm, v(4.1, -26.94) * mm, v(4.55, -26.6) * mm, v(5.22, -26.18) * mm, v(5.48, -26.15) * mm], "startDerivative": vector(-0.87, 3.37) * mm, "endDerivative": vector(1.44, -0.1) * mm});
            skSolve(sketch);
        }
        {
            var Q0;
            Q0=makeQuery(id+"F23.imprint","IMPRINT",FACE,{"disambiguationData":[TD([[makeQuery(id+"F23.imprint","IMPRINT",EDGE,{"derivedFrom":sQuery(id+"F23.wireOp",EDGE,"E71")}),1.0]])]});
            extrude(context, id + "F24", {"entities" : qUnion([Q0]), "operationType" : NewBodyOperationType.ADD, "depth" : 1.25 * mm, "offsetDistance" : 25 * mm});
        }
        {
            var Q0;
            {var subQ0=sQuery(id+"F23.wireOp",EDGE,"E73");Q0=makeQuery(id+"F23.imprint","IMPRINT",FACE,{"disambiguationData":[TD([[makeQuery(id+"F23.imprint","IMPRINT",EDGE,{"derivedFrom":subQ0}),-1.0]])]});}
            extrude(context, id + "F25", {"entities" : qUnion([Q0]), "operationType" : NewBodyOperationType.ADD, "depth" : 2 * mm, "offsetDistance" : 25 * mm});
        }
        {
            var Q0;
            Q0=makeQuery(id+"F3.opExtrude","CAP_FACE",FACE,{"disambiguationData":[OSD([sQuery(id+"F0.wireOp",EDGE,"E18"),sQuery(id+"F0.wireOp",EDGE,"E19"),sQuery(id+"F0.wireOp",EDGE,"E20"),sQuery(id+"F0.wireOp",EDGE,"E21"),sQuery(id+"F0.wireOp",EDGE,"E22"),sQuery(id+"F0.wireOp",EDGE,"E23"),sQuery(id+"F0.wireOp",EDGE,"E24"),sQuery(id+"F0.wireOp",EDGE,"E30"),sQuery(id+"F0.wireOp",EDGE,"E31"),sQuery(id+"F0.wireOp",EDGE,"E32"),sQuery(id+"F0.wireOp",EDGE,"E33"),sQuery(id+"F0.wireOp",EDGE,"E34"),sQuery(id+"F0.wireOp",EDGE,"E35")])],"isStart":false});
            var sketch = newSketch(context, id + "F26", { "sketchPlane" : qUnion([Q0])});
            skFitSpline(sketch, "E76", {"points": [v(-16.64, -22.96) * mm, v(-14.36, -21.57) * mm, v(-10.17, -18.91) * mm], "startDerivative": vector(5, 3.03) * mm, "endDerivative": vector(7.82, 4.98) * mm});
            skFitSpline(sketch, "E77", {"points": [v(-10.17, -18.91) * mm, v(-14.02, -22.29) * mm, v(-15.48, -23.71) * mm], "startDerivative": vector(-7.06, -6.07) * mm, "endDerivative": vector(-3.33, -3.37) * mm});
            skSolve(sketch);
        }
        {
            var Q0;
            {var subQ0=sQuery(id+"F26.wireOp",EDGE,"E76");Q0=makeQuery(id+"F26.imprint","IMPRINT",FACE,{"disambiguationData":[TD([[makeQuery(id+"F26.imprint","IMPRINT",EDGE,{"derivedFrom":subQ0}),-1.0]])]});}
            extrude(context, id + "F27", {"entities" : qUnion([Q0]), "operationType" : NewBodyOperationType.REMOVE, "oppositeDirection" : true, "depth" : 1 * mm, "offsetDistance" : 25 * mm});
        }
    });
